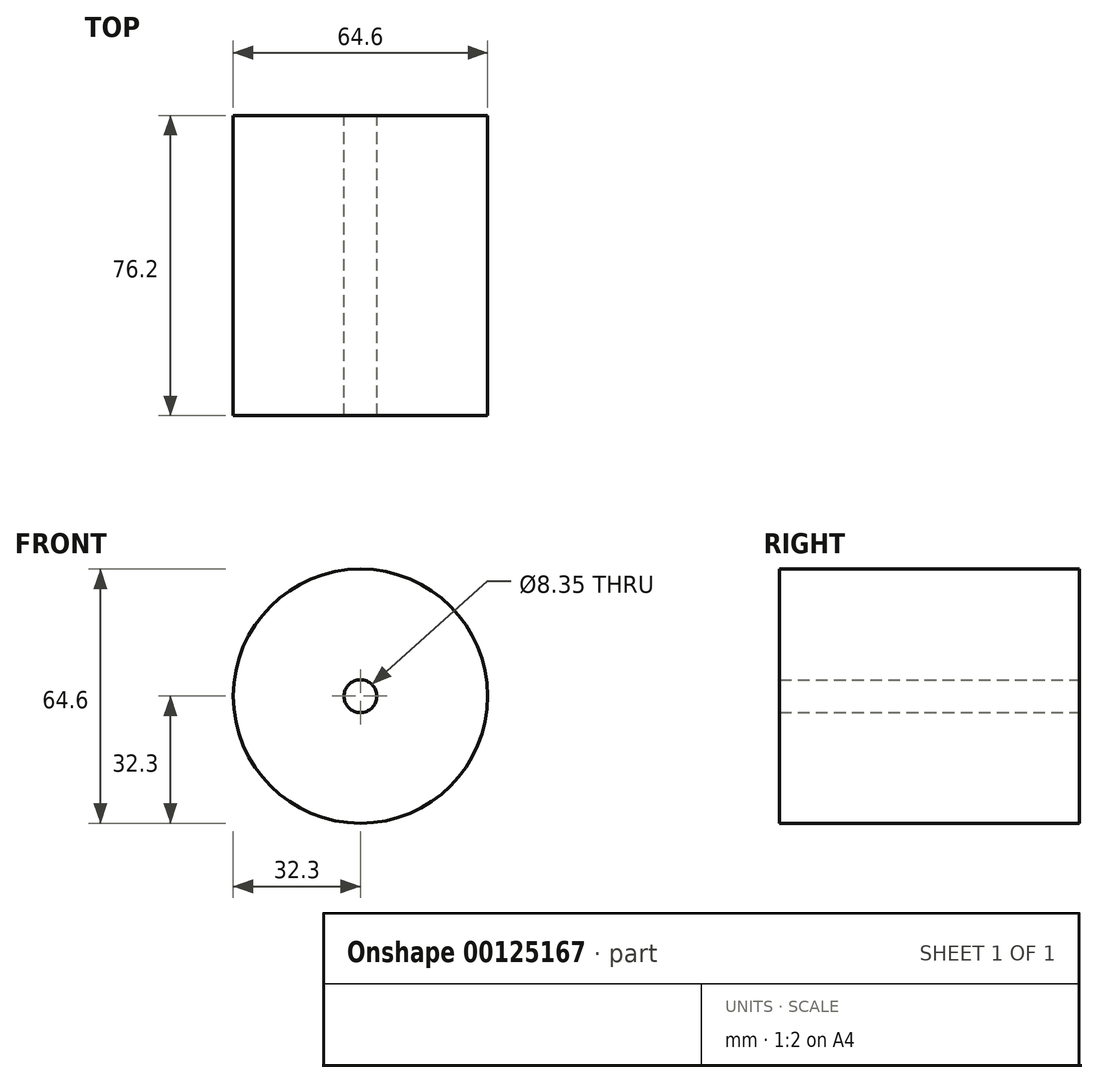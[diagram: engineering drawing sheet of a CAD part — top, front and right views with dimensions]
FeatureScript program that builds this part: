
annotation { "Feature Type Name" : "Feature", "Feature Type Description" : "" }
export const myFeature = defineFeature(function(context is Context, id is Id, definition is map)
    precondition{}
    {
        {
            var Q0;
            Q0=qCreatedBy(makeId("Front.planeOp"),FACE);
            var sketch = newSketch(context, id + "F0", { "sketchPlane" : qUnion([Q0])});
            skCircle(sketch, "E0", {"center": v(0, 0) * mm, "radius": 32.3 * mm});
            skCircle(sketch, "E1", {"center": v(0, 0) * mm, "radius": 4.18 * mm});
            skSolve(sketch);
        }
        {
            var Q0;
            Q0 = qSketchRegion(id + "F0", true);
            extrude(context, id + "F1", {"entities" : qUnion([Q0]), "depth" : 76.2 * mm});
        }
    });
